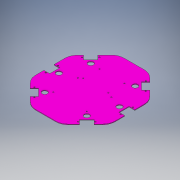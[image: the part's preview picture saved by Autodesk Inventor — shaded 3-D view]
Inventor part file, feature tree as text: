
AUTODESK INVENTOR PART (.ipt)
format: ipt  version: 2019.1 (Build 231200000, 200)  size: 307,200 bytes
history: native  units: in
note: dims shown in document units (in); Inventor stores cm internally (conversion verified against a paired STEP export)
features: extrude x4, sketch x1
ambient origin geometry x8: Origin, YZ Plane, XZ Plane, XY Plane, X Axis, Y Axis, Z Axis, Center Point
bodies: Solid1 (feature_tree)
feature tree (5):
  sketch  "Sketch1"  dims[d0=7.874in d1=7.0866in d2=2.1654in d3=2.1654in d4=2.1654in d5=2.1654in d6=2.1654in d7=2.1654in d8=2.1654in d9=2.1654in d10=0.5118in d11=0.9055in d13=0.5118in d14=0.5118in d15=0.9055in d18=3.0623in d21=0.5118in d22=1.4206in d23=0.4528in d24=0.9055in d25=0.5118in d26=0.9055in d29=0.5118in d30=0.9055in d32=0.0787in d33=1.1811in d34=0.06in d35=0.0in d36=0.1181in d38=0.1181in d39=0.1181in d40=0.1181in d41=0.1181in d43=0.1181in d44=0.1181in d45=0.1181in d46=0.1181in d49=0.2559in d50=0.0915in d53=0.0915in d54=0.2559in d55=0.0917in d56=0.2559in d57=0.0917in d58=0.2559in d60=0.1181in d61=0.2559in d62=0.0917in d63=0.0917in d64=0.2559in d65=0.2559in d66=0.0917in d67=0.2559in d68=0.0917in d69=0.0917in d70=0.2559in d71=0.5118in d72=0.2362in d73=0.0917in d74=0.1181in d75=0.5118in d78=0.0917in d79=0.2559in d80=0.1181in d81=0.2559in d82=0.0917in d83=7.874in d84=0.0in d85=0.3641in d86=0.5118in d87=0.5118in d88=0.5118in d89=0.5118in d90=0.5118in d91=0.5118in d92=0.5118in d93=1.165in d94=2.185in d95=2.9724in d96=0.0984in d97=0.0984in d98=0.0984in d99=0.0984in d100=0.0984in d101=0.0984in d102=0.0984in d103=0.0984in d104=1.437in d105=2.2244in d106=0.2659in d107=0.4821in d108=0.2054in d109=0.4724in d110=0.4724in d111=0.4724in d112=0.4724in d113=0.4724in d114=0.4724in d115=0.3937in d116=0.3937in d117=0.3937in d118=0.3937in d119=0.3937in d120=0.4528in d121=0.4528in d122=0.4528in d123=0.4528in d124=0.4528in d125=0.4528in d126=7.874in d127=0.0in d130=7.874in d131=0.0in]
  extrude  "Extrusion1"  Depth=7.874in
  extrude  "Extrusion2"  Depth=7.874in
  extrude  "Extrusion3"  Depth=7.874in
  extrude  "Extrusion5"  Depth=7.874in
